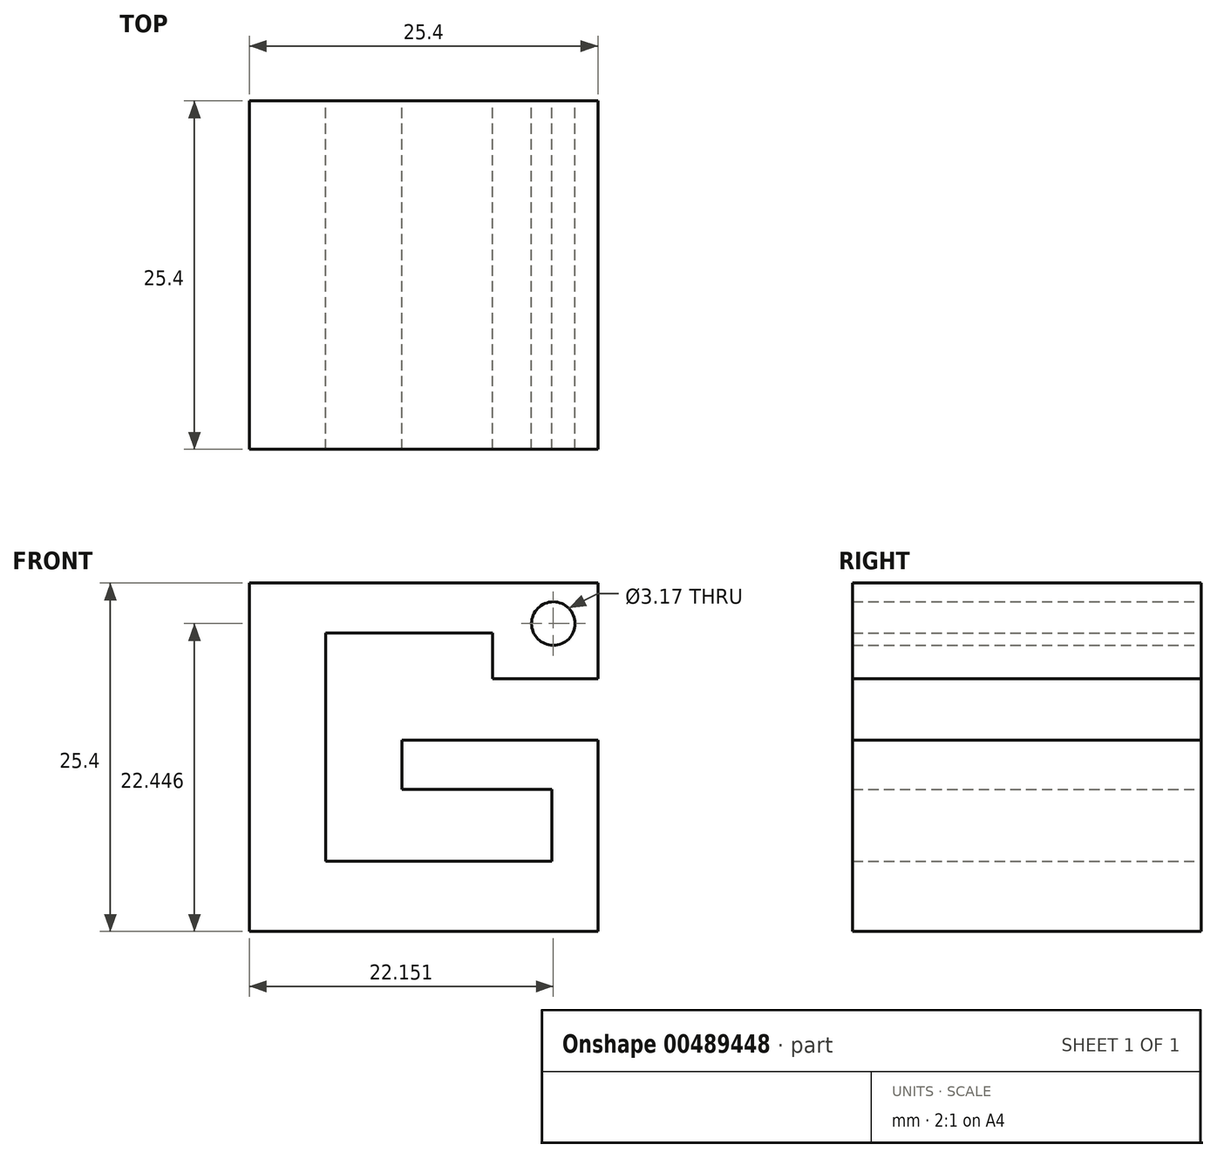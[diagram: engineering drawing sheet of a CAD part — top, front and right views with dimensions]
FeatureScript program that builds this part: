
annotation { "Feature Type Name" : "Feature", "Feature Type Description" : "" }
export const myFeature = defineFeature(function(context is Context, id is Id, definition is map)
    precondition{}
    {
        {
            var Q0;
            Q0=qCreatedBy(makeId("Front.planeOp"),FACE);
            var sketch = newSketch(context, id + "F0", { "sketchPlane" : qUnion([Q0])});
            skLineSegment(sketch, "E0", {"start": v(0, 0) * mm, "end": v(0, 25.4) * mm});
            skLineSegment(sketch, "E1", {"start": v(0, 25.4) * mm, "end": v(25.4, 25.4) * mm});
            skLineSegment(sketch, "E2", {"start": v(25.4, 25.4) * mm, "end": v(25.4, 0) * mm});
            skLineSegment(sketch, "E3", {"start": v(25.4, 0) * mm, "end": v(0, 0) * mm});
            skLineSegment(sketch, "E4", {"start": v(25.4, 9.06) * mm, "end": v(25.4, 0) * mm});
            skLineSegment(sketch, "E5", {"start": v(25.4, 25.4) * mm, "end": v(25.4, 18.43) * mm});
            skLineSegment(sketch, "E6", {"start": v(25.4, 18.43) * mm, "end": v(17.74, 18.43) * mm});
            skLineSegment(sketch, "E7", {"start": v(17.74, 18.43) * mm, "end": v(17.74, 21.75) * mm});
            skLineSegment(sketch, "E8", {"start": v(17.74, 21.75) * mm, "end": v(5.55, 21.75) * mm});
            skLineSegment(sketch, "E9", {"start": v(5.55, 21.75) * mm, "end": v(5.55, 5.13) * mm});
            skLineSegment(sketch, "E10", {"start": v(5.55, 5.13) * mm, "end": v(25.4, 5.13) * mm});
            skPoint(sketch, "E11.start.orphan", {"position": v(25.4, 12.7) * mm});
            skLineSegment(sketch, "E12", {"start": v(25.4, 5.13) * mm, "end": v(25.4, 10.37) * mm});
            skLineSegment(sketch, "E13", {"start": v(25.4, 10.37) * mm, "end": v(11.11, 10.37) * mm});
            skLineSegment(sketch, "E14", {"start": v(11.11, 10.37) * mm, "end": v(11.11, 13.94) * mm});
            skLineSegment(sketch, "E15", {"start": v(11.11, 13.94) * mm, "end": v(25.4, 13.94) * mm});
            skLineSegment(sketch, "E16", {"start": v(22.05, 10.37) * mm, "end": v(22.05, 5.13) * mm});
            skLineSegment(sketch, "E17", {"start": v(25.4, 10.37) * mm, "end": v(25.4, 5.13) * mm});
            skCircle(sketch, "E18", {"center": v(22.15, 22.45) * mm, "radius": 1.59 * mm});
            skSolve(sketch);
        }
        {
            var Q0;
            Q0=makeQuery(id+"F0.imprint","IMPRINT",FACE,{"disambiguationData":[TD([[makeQuery(id+"F0.imprint","IMPRINT",EDGE,{"derivedFrom":sQuery(id+"F0.wireOp",EDGE,"E1")}),-1.0]])]});
            var Q1;
            {var subQ3=sQuery(id+"F0.wireOp",EDGE,"E16");Q1=makeQuery(id+"F0.imprint","IMPRINT",FACE,{"disambiguationData":[TD([[makeQuery(id+"F0.imprint","IMPRINT",EDGE,{"derivedFrom":subQ3}),1.0]])]});}
            var Q2;
            {var subQ0=sQuery(id+"F0.wireOp",EDGE,"E14");Q2=makeQuery(id+"F0.imprint","IMPRINT",FACE,{"disambiguationData":[TD([[makeQuery(id+"F0.imprint","IMPRINT",EDGE,{"derivedFrom":subQ0}),-1.0]])]});}
            extrude(context, id + "F1", {"entities" : qUnion([Q0, Q1, Q2]), "depth" : 25.4 * mm, "offsetDistance" : 25.4 * mm});
        }
    });
